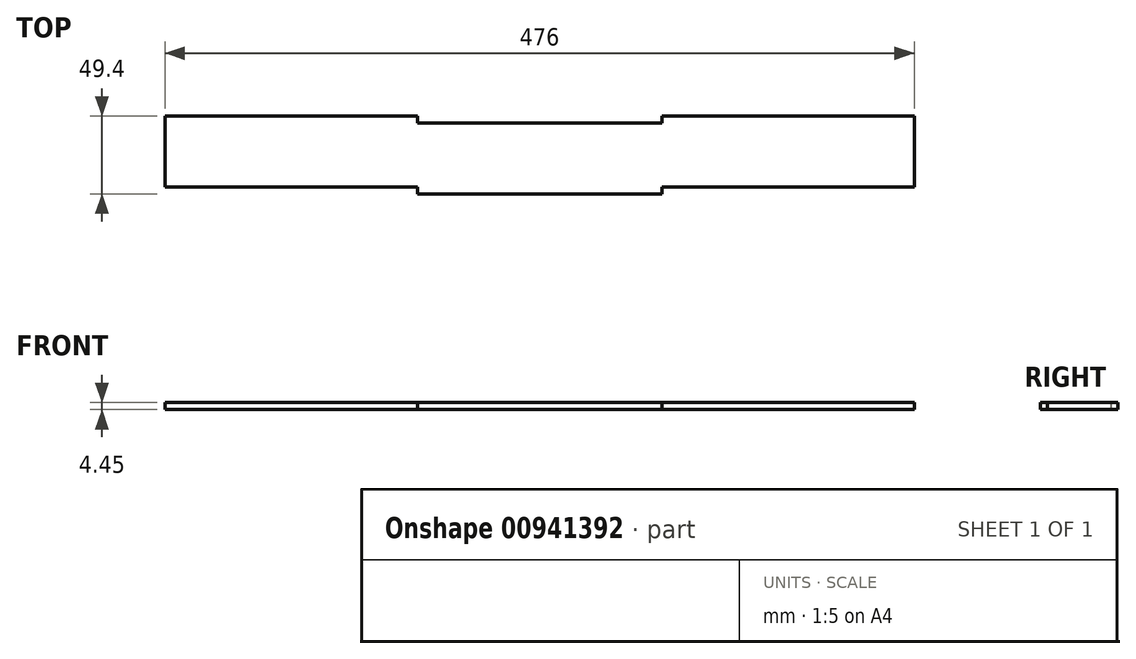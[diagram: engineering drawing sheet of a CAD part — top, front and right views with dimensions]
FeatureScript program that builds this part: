
annotation { "Feature Type Name" : "Feature", "Feature Type Description" : "" }
export const myFeature = defineFeature(function(context is Context, id is Id, definition is map)
    precondition{}
    {
        {
            var Q0;
            Q0=qCreatedBy(makeId("Top.planeOp"),FACE);
            var sketch = newSketch(context, id + "F0", { "sketchPlane" : qUnion([Q0])});
            skLineSegment(sketch, "E0.bottom", {"start": v(-62, 27.68) * mm, "end": v(93.16, 27.68) * mm});
            skLineSegment(sketch, "E0.top", {"start": v(-222.42, -12.82) * mm, "end": v(-62, -12.82) * mm});
            skLineSegment(sketch, "E0.left", {"start": v(-222.42, 27.68) * mm, "end": v(-222.42, -12.82) * mm});
            skLineSegment(sketch, "E0.right", {"start": v(253.58, 27.68) * mm, "end": v(253.58, -12.82) * mm});
            skLineSegment(sketch, "E1.top", {"start": v(93.16, 27.68) * mm, "end": v(-62, 27.68) * mm});
            skLineSegment(sketch, "E2.top", {"start": v(-222.42, 32.13) * mm, "end": v(-62, 32.13) * mm});
            skLineSegment(sketch, "E2.left", {"start": v(-222.42, 27.68) * mm, "end": v(-222.42, 32.13) * mm});
            skLineSegment(sketch, "E2.right", {"start": v(-62, 27.68) * mm, "end": v(-62, 32.13) * mm});
            skLineSegment(sketch, "E3.MirrorCS", {"start": v(93.16, 27.68) * mm, "end": v(93.16, 32.13) * mm});
            skLineSegment(sketch, "E4.MirrorCS", {"start": v(253.58, 32.13) * mm, "end": v(93.16, 32.13) * mm});
            skLineSegment(sketch, "E5.MirrorCS", {"start": v(253.58, 27.68) * mm, "end": v(253.58, 32.13) * mm});
            skLineSegment(sketch, "E6.top", {"start": v(-62, -17.27) * mm, "end": v(93.16, -17.27) * mm});
            skLineSegment(sketch, "E6.left", {"start": v(-62, -12.82) * mm, "end": v(-62, -17.27) * mm});
            skLineSegment(sketch, "E6.right", {"start": v(93.16, -12.82) * mm, "end": v(93.16, -17.27) * mm});
            skLineSegment(sketch, "E7.trimOffspring", {"start": v(93.16, -12.82) * mm, "end": v(253.58, -12.82) * mm});
            skSolve(sketch);
        }
        {
            var Q0;
            Q0 = qSketchRegion(id + "F0", true);
            extrude(context, id + "F1", {"entities" : qUnion([Q0]), "depth" : 4.45 * mm, "offsetDistance" : 25 * mm});
        }
    });
